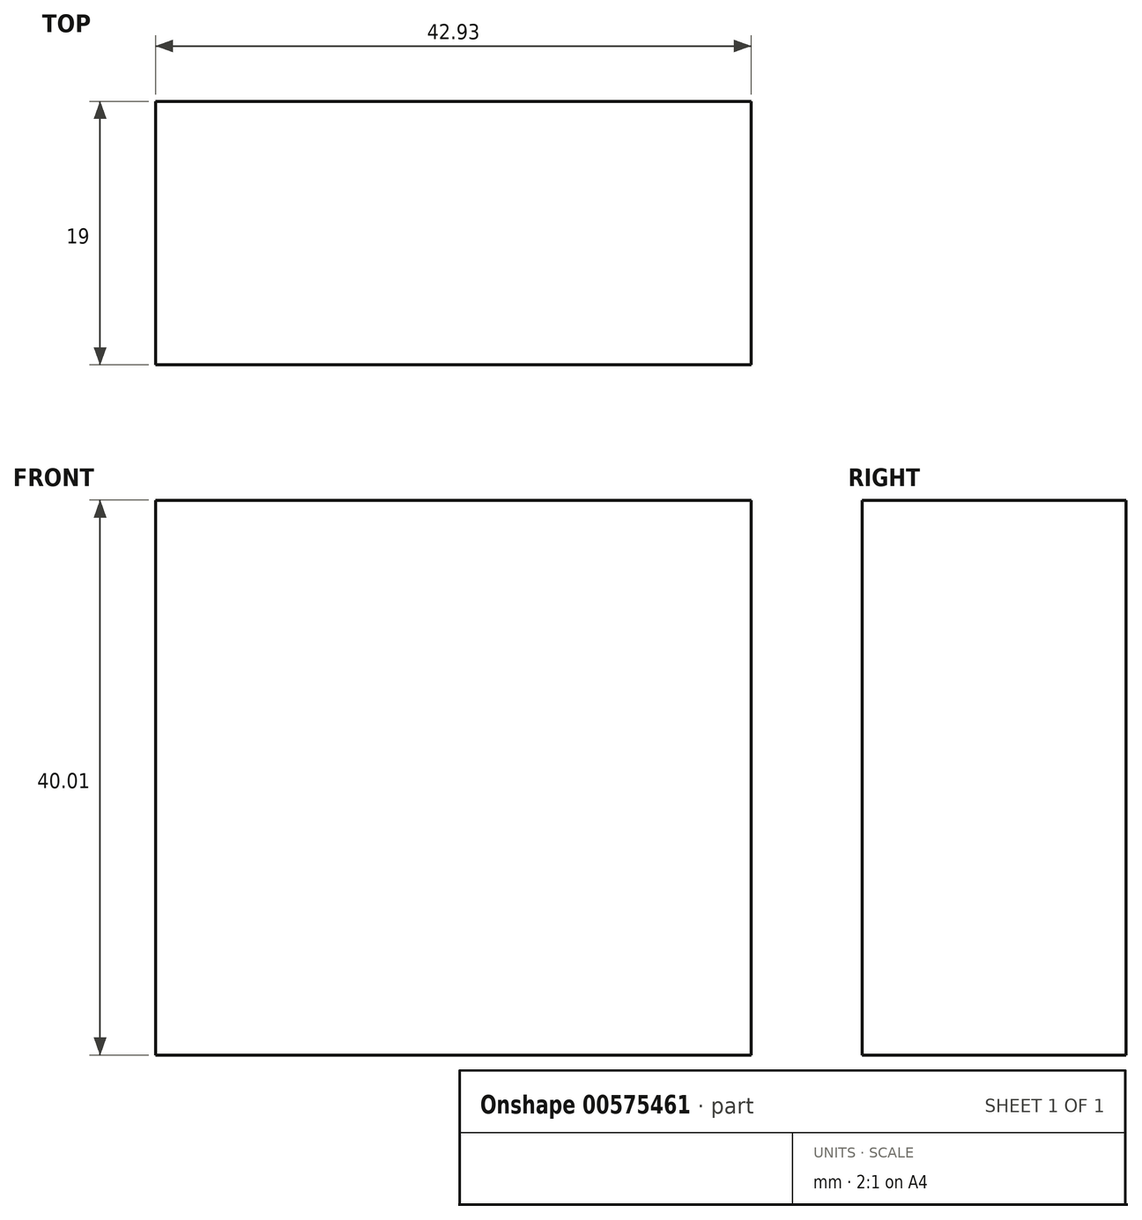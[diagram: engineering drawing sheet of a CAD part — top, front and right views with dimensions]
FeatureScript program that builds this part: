
annotation { "Feature Type Name" : "Feature", "Feature Type Description" : "" }
export const myFeature = defineFeature(function(context is Context, id is Id, definition is map)
    precondition{}
    {
        {
            var Q0;
            Q0=qCreatedBy(makeId("Front.planeOp"),FACE);
            var sketch = newSketch(context, id + "F0", { "sketchPlane" : qUnion([Q0])});
            skLineSegment(sketch, "E0.bottom", {"start": v(-129.51, 87.7) * mm, "end": v(-86.58, 87.7) * mm});
            skLineSegment(sketch, "E0.top", {"start": v(-129.51, 47.7) * mm, "end": v(-86.58, 47.7) * mm});
            skLineSegment(sketch, "E0.left", {"start": v(-129.51, 87.7) * mm, "end": v(-129.51, 47.7) * mm});
            skLineSegment(sketch, "E0.right", {"start": v(-86.58, 87.7) * mm, "end": v(-86.58, 47.7) * mm});
            skSolve(sketch);
        }
        {
            var Q0;
            Q0=makeQuery(id+"F0.imprint","IMPRINT",FACE,{"disambiguationData":[TD([[makeQuery(id+"F0.imprint","IMPRINT",EDGE,{"derivedFrom":sQuery(id+"F0.wireOp",EDGE,"E0.bottom")}),-1.0]])]});
            extrude(context, id + "F1", {"entities" : qUnion([Q0]), "depth" : 19 * mm, "offsetDistance" : 25.4 * mm});
        }
    });
